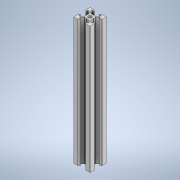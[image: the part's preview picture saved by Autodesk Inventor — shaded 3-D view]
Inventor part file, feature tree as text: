
AUTODESK INVENTOR PART (.ipt)
format: ipt  version: 2021 (Build 250183000, 183)  size: 233,984 bytes
history: native  units: mm
features: sketch x3, extrude x2, fillet x2, other x1, pattern_circular x1, hole x1, projected_geometry x1
ambient origin geometry x8: Origin, YZ Plane, XZ Plane, XY Plane, X Axis, Y Axis, Z Axis, Center Point
bodies: Body1 (feature_tree)
feature tree (11):
  other  "實體1"
  extrude  "擠出1"  Depth=20.0mm
  extrude  "擠出2"  Depth=20.0mm
  fillet  "圓角1"  Radius=156.0mm
  pattern_circular  "環形陣列1"  [2 undecoded]
  hole  "孔1"  [1 undecoded]
  fillet  "圓角2"  Radius=6.2mm
  sketch  "草圖1"
  sketch  "草圖2"
  projected_geometry  "投影迴路1"
  sketch  "草圖3"
note: 3 required parameter values undecoded (feature->parameter linkage not recoverable at this tier; creation-order binding heuristic only, values carry confidence <= 0.55)
